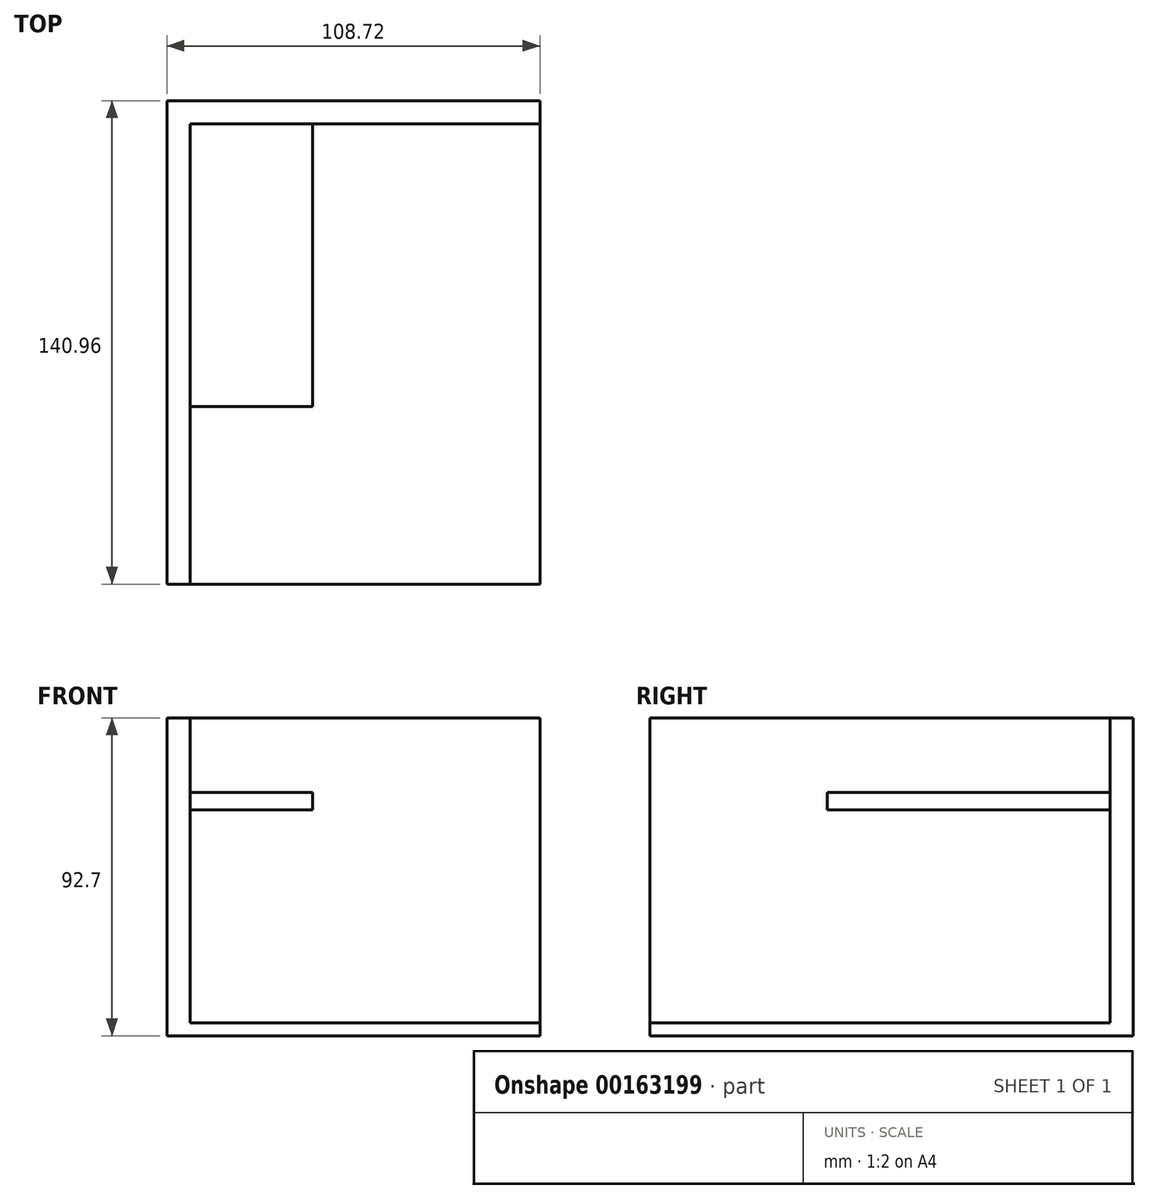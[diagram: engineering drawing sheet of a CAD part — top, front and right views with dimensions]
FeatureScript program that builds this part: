
annotation { "Feature Type Name" : "Feature", "Feature Type Description" : "" }
export const myFeature = defineFeature(function(context is Context, id is Id, definition is map)
    precondition{}
    {
        {
            var Q0;
            Q0=qCreatedBy(makeId("Top.planeOp"),FACE);
            var sketch = newSketch(context, id + "F0", { "sketchPlane" : qUnion([Q0])});
            skLineSegment(sketch, "E0.bottom", {"start": v(-47.56, 63.68) * mm, "end": v(47.56, 63.68) * mm});
            skLineSegment(sketch, "E0.top", {"start": v(-47.56, -63.68) * mm, "end": v(47.56, -63.68) * mm});
            skLineSegment(sketch, "E0.left", {"start": v(-47.56, 63.68) * mm, "end": v(-47.56, -63.68) * mm});
            skLineSegment(sketch, "E0.right", {"start": v(47.56, 63.68) * mm, "end": v(47.56, -63.68) * mm});
            skPoint(sketch, "E0.middle", {"position": v(0, 0) * mm});
            skLineSegment(sketch, "E1.0", {"start": v(-54.36, 70.48) * mm, "end": v(-54.36, -70.48) * mm});
            skLineSegment(sketch, "E1.1", {"start": v(-54.36, 70.48) * mm, "end": v(54.36, 70.48) * mm});
            skLineSegment(sketch, "E1.2", {"start": v(54.36, 70.48) * mm, "end": v(54.36, -70.48) * mm});
            skLineSegment(sketch, "E1.3", {"start": v(-54.36, -70.48) * mm, "end": v(54.36, -70.48) * mm});
            skSolve(sketch);
        }
        {
            var Q0;
            Q0 = qSketchRegion(id + "F0", true);
            extrude(context, id + "F1", {"entities" : qUnion([Q0]), "depth" : 88.9 * mm});
        }
        {
            var Q0;
            Q0=makeQuery(id+"F1.opExtrude","CAP_FACE",FACE,{"disambiguationData":[OSD([sQuery(id+"F0.wireOp",EDGE,"E0.bottom"),sQuery(id+"F0.wireOp",EDGE,"E0.top"),sQuery(id+"F0.wireOp",EDGE,"E0.left"),sQuery(id+"F0.wireOp",EDGE,"E0.right"),sQuery(id+"F0.wireOp",EDGE,"E1.0"),sQuery(id+"F0.wireOp",EDGE,"E1.1"),sQuery(id+"F0.wireOp",EDGE,"E1.2"),sQuery(id+"F0.wireOp",EDGE,"E1.3")])],"isStart":true});
            var sketch = newSketch(context, id + "F2", { "sketchPlane" : qUnion([Q0])});
            skLineSegment(sketch, "E2.0", {"start": v(-54.36, 70.48) * mm, "end": v(54.36, 70.48) * mm});
            skLineSegment(sketch, "E3.0", {"start": v(-54.36, -70.48) * mm, "end": v(-54.36, 70.48) * mm});
            skLineSegment(sketch, "E4.0", {"start": v(54.36, -70.48) * mm, "end": v(54.36, 70.48) * mm});
            skLineSegment(sketch, "E5.0", {"start": v(-54.36, -70.48) * mm, "end": v(54.36, -70.48) * mm});
            skSolve(sketch);
        }
        {
            var Q0;
            Q0 = qSketchRegion(id + "F2", true);
            extrude(context, id + "F3", {"entities" : qUnion([Q0]), "operationType" : NewBodyOperationType.ADD, "depth" : 3.8 * mm});
        }
        {
            var Q0;
            Q0=makeQuery(id+"F1.opExtrude","CAP_FACE",FACE,{"disambiguationData":[OSD([sQuery(id+"F0.wireOp",EDGE,"E0.bottom"),sQuery(id+"F0.wireOp",EDGE,"E0.top"),sQuery(id+"F0.wireOp",EDGE,"E0.left"),sQuery(id+"F0.wireOp",EDGE,"E0.right"),sQuery(id+"F0.wireOp",EDGE,"E1.0"),sQuery(id+"F0.wireOp",EDGE,"E1.1"),sQuery(id+"F0.wireOp",EDGE,"E1.2"),sQuery(id+"F0.wireOp",EDGE,"E1.3")])],"isStart":false});
            var sketch = newSketch(context, id + "F4", { "sketchPlane" : qUnion([Q0])});
            skLineSegment(sketch, "E6.bottom", {"start": v(54.36, -70.48) * mm, "end": v(-47.56, -70.48) * mm});
            skLineSegment(sketch, "E6.top", {"start": v(54.36, 63.68) * mm, "end": v(-47.56, 63.68) * mm});
            skLineSegment(sketch, "E6.left", {"start": v(54.36, -70.48) * mm, "end": v(54.36, 63.68) * mm});
            skLineSegment(sketch, "E6.right", {"start": v(-47.56, -70.48) * mm, "end": v(-47.56, 63.68) * mm});
            skSolve(sketch);
        }
        {
            var Q0;
            Q0 = qSketchRegion(id + "F4", true);
            var Q1;
            Q1=makeQuery(id+"F3.opExtrude","CAP_FACE",FACE,{"disambiguationData":[OSD([sQuery(id+"F2.wireOp",EDGE,"E2.0"),sQuery(id+"F2.wireOp",EDGE,"E3.0"),sQuery(id+"F2.wireOp",EDGE,"E4.0"),sQuery(id+"F2.wireOp",EDGE,"E5.0")])],"isStart":true});
            extrude(context, id + "F5", {"entities" : qUnion([Q0]), "operationType" : NewBodyOperationType.REMOVE, "endBound" : BoundingType.UP_TO_SURFACE, "oppositeDirection" : true, "endBoundEntityFace" : qUnion([Q1]), "depth" : 25 * mm});
        }
        {
            var Q0;
            Q0=makeQuery(id+"F5.boolean.opBoolean","MERGE",FACE,{"derivedFrom":[makeQuery(id+"F1.opExtrude","SWEPT_FACE",FACE,{"disambiguationData":[OSD([sQuery(id+"F0.wireOp",EDGE,"E0.bottom")])]}),makeQuery(id+"F5.opExtrude","SWEPT_FACE",FACE,{"disambiguationData":[OSD([sQuery(id+"F4.wireOp",EDGE,"E6.top")])]})]});
            var sketch = newSketch(context, id + "F6", { "sketchPlane" : qUnion([Q0])});
            skLineSegment(sketch, "E7.bottom", {"start": v(-47.56, 67.13) * mm, "end": v(-11.93, 67.13) * mm});
            skLineSegment(sketch, "E7.top", {"start": v(-47.56, 62.12) * mm, "end": v(-11.93, 62.12) * mm});
            skLineSegment(sketch, "E7.left", {"start": v(-47.56, 67.13) * mm, "end": v(-47.56, 62.12) * mm});
            skLineSegment(sketch, "E7.right", {"start": v(-11.93, 67.13) * mm, "end": v(-11.93, 62.12) * mm});
            skSolve(sketch);
        }
        {
            var Q0;
            Q0 = qSketchRegion(id + "F6", true);
            extrude(context, id + "F7", {"entities" : qUnion([Q0]), "operationType" : NewBodyOperationType.ADD, "depth" : 82.4 * mm});
        }
    });
